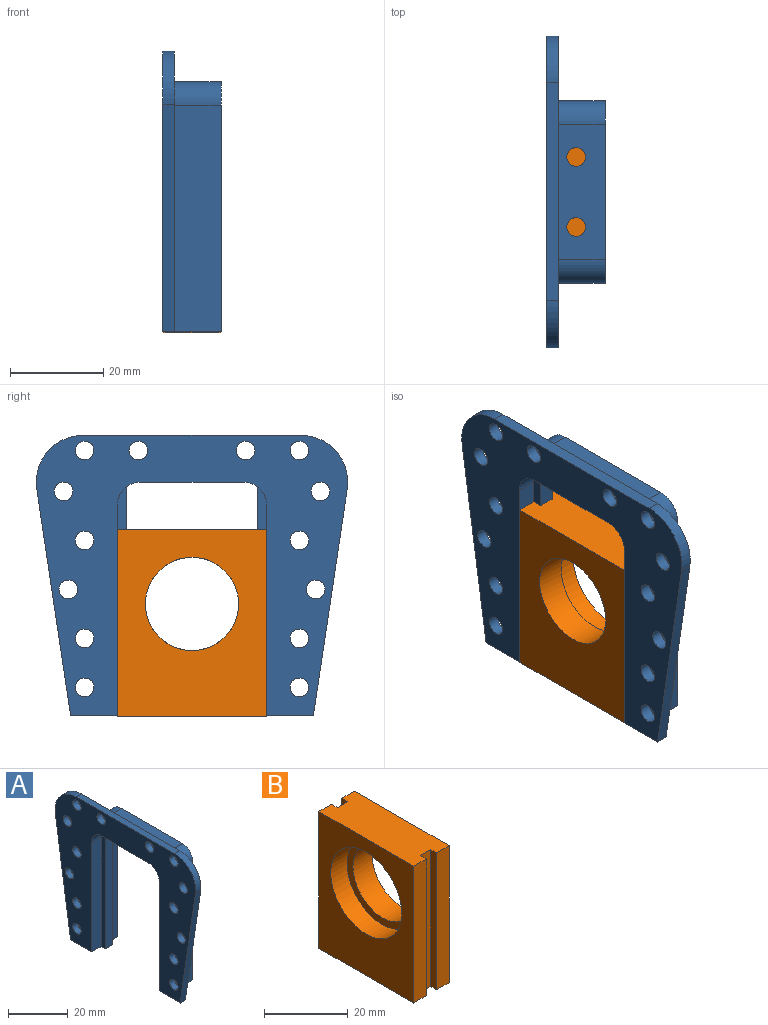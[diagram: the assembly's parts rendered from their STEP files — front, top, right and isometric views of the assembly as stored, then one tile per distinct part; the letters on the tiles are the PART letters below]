
ASSEMBLY  parts=2 mates=1
PART A: 44 faces, bbox 12.5x66.7x60 mm
  f0: plane 22x12.5mm, normal (0,0,-1), area 249.9mm2, adj f3,f15,f16,f21,f42,f43
  f1: plane 29x10mm, normal (0,0,1), area 264.9mm2, adj f2,f19,f20,f21,f42,f43
  f2: plane 66.74x60mm, normal (1,0,0), area 1346.6mm2, adj f1,f8,f9,f10,f11,f12,f13,f14
  f3: plane 66.74x60mm, normal (-1,0,0), area 1833.1mm2, adj f0,f6,f7,f8,f9,f10,f11,f12
  f4: plane 45x4.5mm, normal (0,1,0), area 202.5mm2, adj f14,f15,f21,f26
  f5: plane 45x4.5mm, normal (0,-1,0), area 202.5mm2, adj f8,f16,f21,f22
  f6: plane 45x4.5mm, normal (0,1,0), area 202.5mm2, adj f3,f14,f15,f25
  f7: plane 45x4.5mm, normal (0,-1,0), area 202.5mm2, adj f3,f8,f16,f23
  f8: plane 12.5x12mm, normal (0,0,-1), area 67mm2, adj f2,f3,f5,f7,f9,f18,f21,f22
  f9: plane 48.52x7.26mm, normal (0,0.99,-0.15), area 122.7mm2, adj f2,f3,f8,f10
  f10: cylinder r=10mm len=11.48mm, axis (-1,0,0), area 43mm2, adj f2,f3,f9,f11
  f11: plane 46.74x2.5mm, normal (0,0,1), area 116.8mm2, adj f2,f3,f10,f12
  f12: cylinder r=10mm len=11.48mm, axis (-1,0,0), area 43mm2, adj f2,f3,f11,f13
  f13: plane 48.52x7.26mm, normal (0,-0.99,-0.15), area 122.7mm2, adj f2,f3,f12,f14
  f14: plane 12.5x12mm, normal (0,0,-1), area 67mm2, adj f2,f3,f4,f6,f13,f17,f21,f25
  f15: cylinder r=5mm len=12.5mm, axis (-1,0,0), area 81.9mm2, adj f0,f3,f4,f6,f21,f25,f26,f27
  f16: cylinder r=5mm len=12.5mm, axis (1,0,0), area 81.9mm2, adj f0,f3,f5,f7,f21,f22,f23,f24
  f17: plane 48.5x10mm, normal (0,-1,0), area 485mm2, adj f2,f14,f20,f21
  f18: plane 48.5x10mm, normal (0,1,0), area 485mm2, adj f2,f8,f19,f21
  f19: cylinder r=5mm len=10mm, axis (-1,0,0), area 78.5mm2, adj f1,f2,f18,f21
  f20: cylinder r=5mm len=10mm, axis (-1,0,0), area 78.5mm2, adj f1,f2,f17,f21
  f21: plane 53.5x39mm, normal (1,0,0), area 486.5mm2, adj f0,f1,f4,f5,f8,f14,f15,f16
  f22: plane 49x2mm, normal (1,0,0), area 95.6mm2, adj f5,f8,f16,f24
  f23: plane 49x2mm, normal (-1,0,0), area 95.6mm2, adj f7,f8,f16,f24
  f24: plane 49x3.5mm, normal (0,-1,0), area 171.5mm2, adj f8,f16,f22,f23
  f25: plane 49x2mm, normal (-1,0,0), area 95.6mm2, adj f6,f14,f15,f27
  f26: plane 49x2mm, normal (1,0,0), area 95.6mm2, adj f4,f14,f15,f27
  f27: plane 49x3.5mm, normal (0,1,0), area 171.5mm2, adj f14,f15,f25,f26
  f28: cylinder r=2mm len=4mm, axis (1,0,0), area 31.4mm2, adj f2,f3
  f29: cylinder r=2mm len=4mm, axis (1,0,0), area 31.4mm2, adj f2,f3
  f30: cylinder r=2mm len=4mm, axis (1,0,0), area 31.4mm2, adj f2,f3
  f31: cylinder r=2mm len=4mm, axis (1,0,0), area 31.4mm2, adj f2,f3
  f32: cylinder r=2mm len=4mm, axis (1,0,0), area 31.4mm2, adj f2,f3
  f33: cylinder r=2mm len=4mm, axis (1,0,0), area 31.4mm2, adj f2,f3
  f34: cylinder r=2mm len=4mm, axis (1,0,0), area 31.4mm2, adj f2,f3
  f35: cylinder r=2mm len=4mm, axis (1,0,0), area 31.4mm2, adj f2,f3
  f36: cylinder r=2mm len=4mm, axis (1,0,0), area 31.4mm2, adj f2,f3
  f37: cylinder r=2mm len=4mm, axis (1,0,0), area 31.4mm2, adj f2,f3
  f38: cylinder r=2mm len=4mm, axis (1,0,0), area 31.4mm2, adj f2,f3
  f39: cylinder r=2mm len=4mm, axis (1,0,0), area 31.4mm2, adj f2,f3
  f40: cylinder r=2mm len=4mm, axis (1,0,0), area 31.4mm2, adj f2,f3
  f41: cylinder r=2mm len=4mm, axis (1,0,0), area 31.4mm2, adj f2,f3
  f42: cylinder r=2mm len=4mm, axis (0,0,1), area 44mm2, adj f0,f1
  f43: cylinder r=2mm len=4mm, axis (0,0,1), area 44mm2, adj f0,f1
PART B: 17 faces, bbox 12x32x40 mm
  f0: cylinder r=10mm len=20mm, axis (-1,0,0), area 408.4mm2, adj f7,f16
  f1: plane 40x4.25mm, normal (0,-1,0), area 170mm2, adj f3,f5,f7,f9
  f2: plane 40x4.25mm, normal (0,1,0), area 170mm2, adj f3,f5,f7,f14
  f3: plane 32x12mm, normal (0,0,1), area 370mm2, adj f1,f2,f4,f6,f7,f8,f9,f10
  f4: plane 40x4.25mm, normal (0,-1,0), area 170mm2, adj f3,f5,f8,f11
  f5: plane 32x12mm, normal (0,0,-1), area 370mm2, adj f1,f2,f4,f6,f7,f8,f9,f10
  f6: plane 40x4.25mm, normal (0,1,0), area 170mm2, adj f3,f5,f8,f12
  f7: plane 40x32mm, normal (1,0,0), area 965.8mm2, adj f0,f1,f2,f3,f5
  f8: plane 40x32mm, normal (-1,0,0), area 827.6mm2, adj f3,f4,f5,f6,f15
  f9: plane 40x2mm, normal (-1,0,0), area 80mm2, adj f1,f3,f5,f10
  f10: plane 40x3.5mm, normal (0,-1,0), area 140mm2, adj f3,f5,f9,f11
  f11: plane 40x2mm, normal (1,0,0), area 80mm2, adj f3,f4,f5,f10
  f12: plane 40x2mm, normal (1,0,0), area 80mm2, adj f3,f5,f6,f13
  f13: plane 40x3.5mm, normal (0,1,0), area 140mm2, adj f3,f5,f12,f14
  f14: plane 40x2mm, normal (-1,0,0), area 80mm2, adj f2,f3,f5,f13
  f15: cylinder r=12mm len=24mm, axis (-1,0,0), area 414.7mm2, adj f8,f16
  f16: plane 24x24mm, normal (-1,0,0), area 138.2mm2, adj f0,f15
PLACE A t=(22.25,-1.48,-15.2)mm fixed
PLACE B rot(axis=(0,0,1),180deg) t=(34.5,17.84,-25.59)mm
MATE slider B.f3 <-> A.f0  axis (0,0,1) through (28.5,11.21,-27.81)mm
